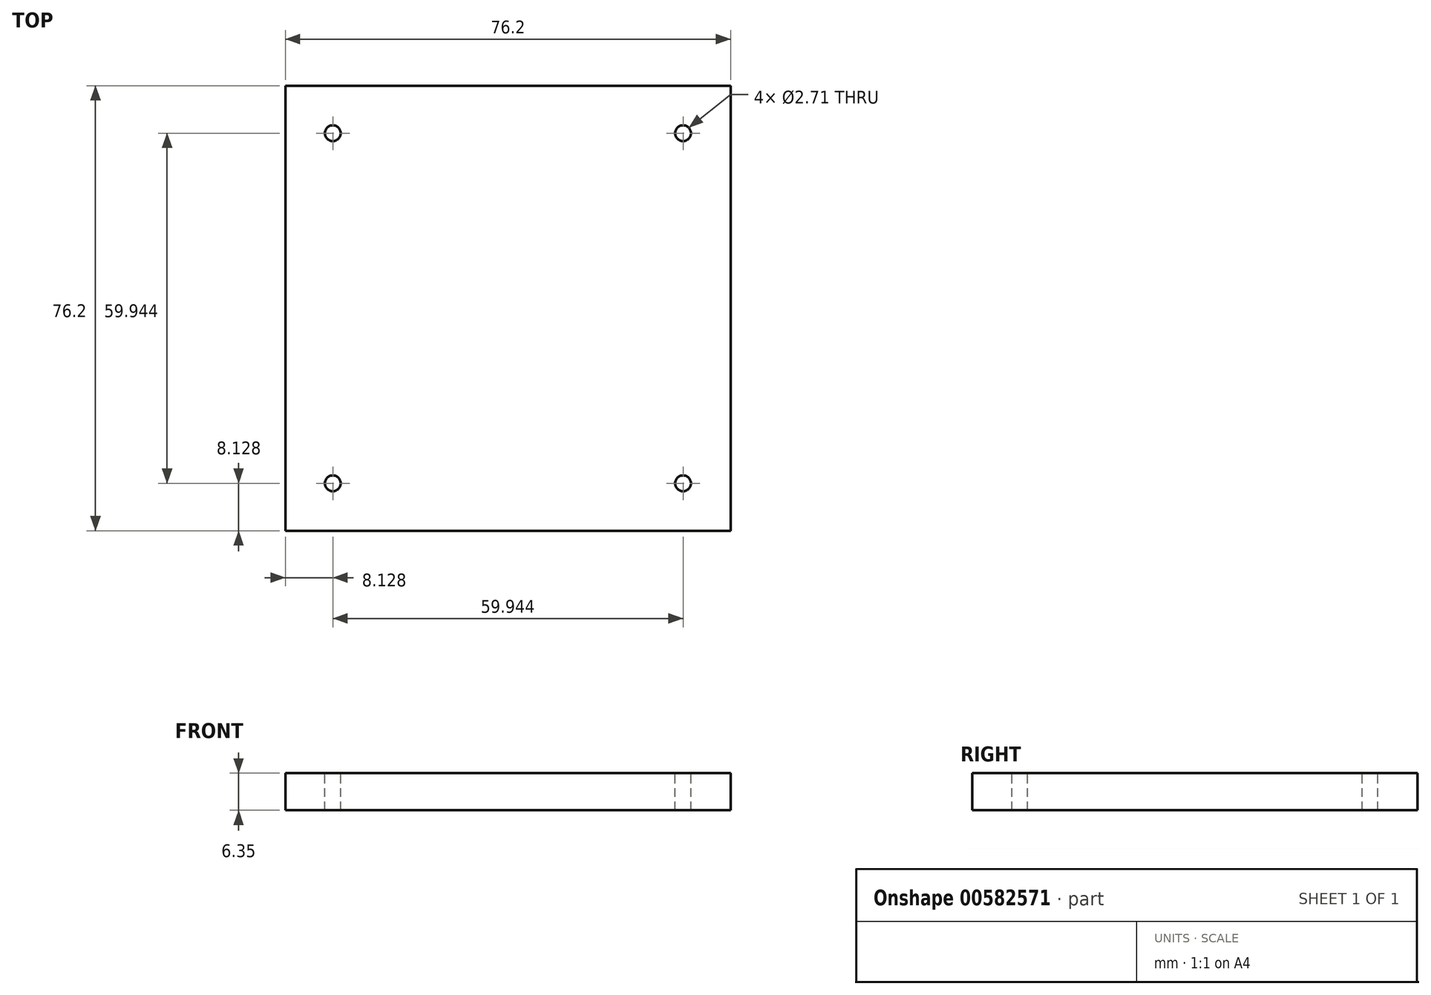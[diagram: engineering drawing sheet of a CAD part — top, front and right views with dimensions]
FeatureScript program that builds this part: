
annotation { "Feature Type Name" : "Feature", "Feature Type Description" : "" }
export const myFeature = defineFeature(function(context is Context, id is Id, definition is map)
    precondition{}
    {
        {
            var Q0;
            Q0=qCreatedBy(makeId("Top.planeOp"),FACE);
            var sketch = newSketch(context, id + "F0", { "sketchPlane" : qUnion([Q0])});
            skLineSegment(sketch, "E0.bottom", {"start": v(-38.1, 38.1) * mm, "end": v(38.1, 38.1) * mm});
            skLineSegment(sketch, "E0.top", {"start": v(-38.1, -38.1) * mm, "end": v(38.1, -38.1) * mm});
            skLineSegment(sketch, "E0.left", {"start": v(-38.1, 38.1) * mm, "end": v(-38.1, -38.1) * mm});
            skLineSegment(sketch, "E0.right", {"start": v(38.1, 38.1) * mm, "end": v(38.1, -38.1) * mm});
            skSolve(sketch);
        }
        {
            var Q0;
            Q0=makeQuery(id+"F0.imprint","IMPRINT",FACE,{"disambiguationData":[TD([[makeQuery(id+"F0.imprint","IMPRINT",EDGE,{"derivedFrom":sQuery(id+"F0.wireOp",EDGE,"E0.bottom")}),-1.0]])]});
            var Q1;
            Q1=sQuery(id+"F0.wireOp",EDGE,"E0.right");
            var Q2;
            Q2=sQuery(id+"F0.wireOp",EDGE,"E0.bottom");
            var Q3;
            Q3=sQuery(id+"F0.wireOp",EDGE,"E0.left");
            var Q4;
            Q4=sQuery(id+"F0.wireOp",EDGE,"E0.top");
            extrude(context, id + "F1", {"entities" : qUnion([Q0]), "surfaceEntities" : qUnion([Q1, Q2, Q3, Q4]), "depth" : 6.35 * mm, "offsetDistance" : 25.4 * mm});
        }
        {
            var Q0;
            Q0=makeQuery(id+"F1.opExtrude","CAP_FACE",FACE,{"disambiguationData":[OSD([sQuery(id+"F0.wireOp",EDGE,"E0.bottom"),sQuery(id+"F0.wireOp",EDGE,"E0.top"),sQuery(id+"F0.wireOp",EDGE,"E0.left"),sQuery(id+"F0.wireOp",EDGE,"E0.right")])],"isStart":false});
            var sketch = newSketch(context, id + "F2", { "sketchPlane" : qUnion([Q0])});
            skPoint(sketch, "E1", {"position": v(-29.97, 29.97) * mm});
            skPoint(sketch, "E2.MirrorP", {"position": v(29.97, 29.97) * mm});
            skPoint(sketch, "E3.MirrorP", {"position": v(-29.97, -29.97) * mm});
            skPoint(sketch, "E4.MirrorP", {"position": v(29.97, -29.97) * mm});
            skSolve(sketch);
        }
        {
            var Q0;
            Q0=sQuery(id+"F2.wireOp",VERTEX,"E1");
            var Q1;
            Q1=sQuery(id+"F2.wireOp",VERTEX,"E2.MirrorP");
            var Q2;
            Q2=sQuery(id+"F2.wireOp",VERTEX,"E4.MirrorP");
            var Q3;
            Q3=sQuery(id+"F2.wireOp",VERTEX,"E3.MirrorP");
            var Q4;
            Q4=makeQuery(id+"F1.opExtrude","SWEPT_BODY",BODY,{"disambiguationData":[OSD([sQuery(id+"F0.wireOp",EDGE,"E0.bottom"),sQuery(id+"F0.wireOp",EDGE,"E0.top"),sQuery(id+"F0.wireOp",EDGE,"E0.left"),sQuery(id+"F0.wireOp",EDGE,"E0.right")])]});
            hole(context, id + "F3", {"style" : HoleStyle.SIMPLE, "endStyle" : HoleEndStyle.THROUGH, "standardTappedOrClearance" : lookupTablePath({ "standard" : "ANSI", "engagement" : "75%", "pitch" : "32 tpi", "size" : "#6", "type" : "Tapped" }), "standardBlindInLast" : lookupTablePath({ "standard" : "ANSI", "engagement" : "75%", "pitch" : "32 tpi", "size" : "#6", "type" : "Tapped" }), "holeDiameter" : 2.7 * mm, "majorDiameter" : 3.5 * mm, "showTappedDepth" : true, "isTappedThrough" : true, "tappedDepth" : 12.7 * mm, "tapClearance" : 3, "locations" : qUnion([Q0, Q1, Q2, Q3]), "scope" : qUnion([Q4])});
        }
    });
